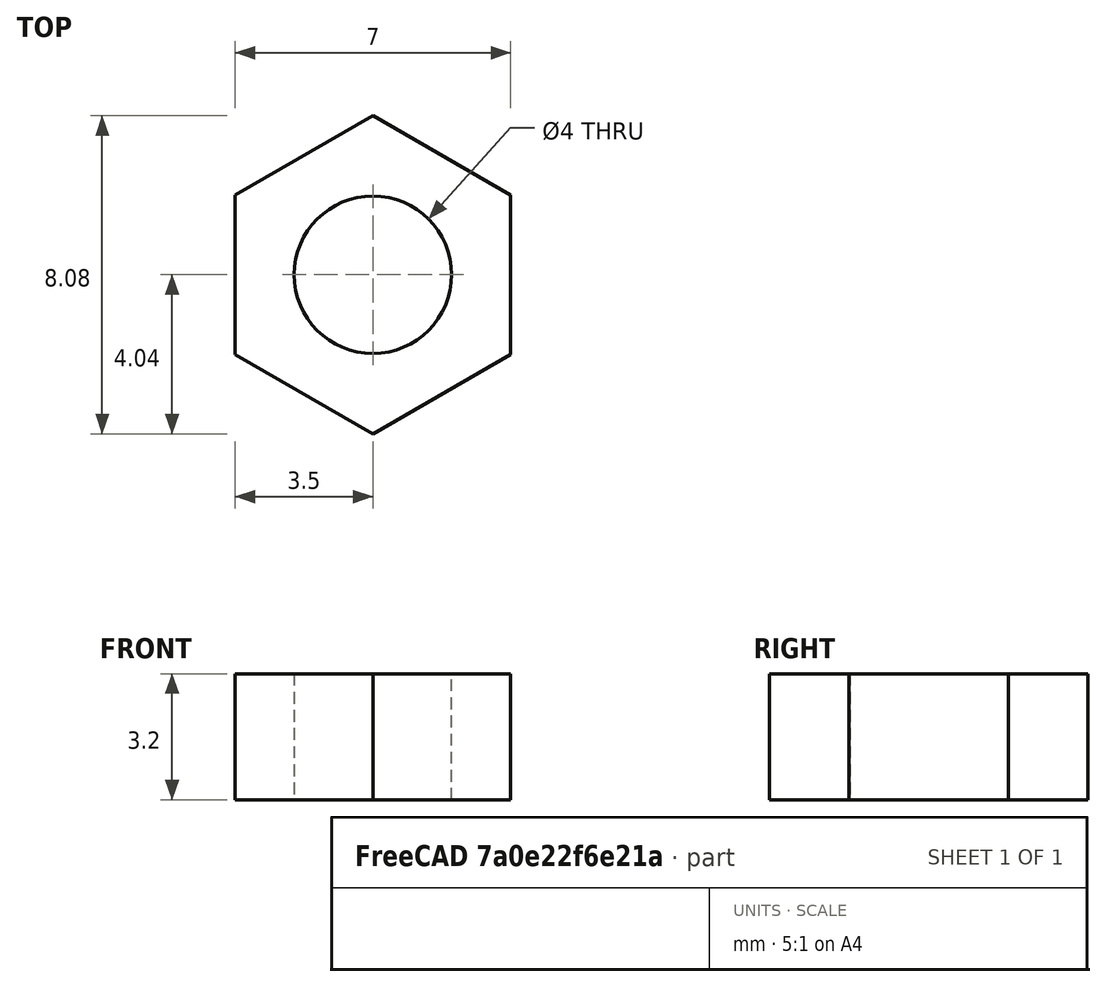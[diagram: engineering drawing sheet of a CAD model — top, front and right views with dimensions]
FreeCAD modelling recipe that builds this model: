
FCSTD DOCUMENT  (FreeCAD 0.18R14555 (Git shallow))
Label: m4-nut
License: All rights reserved
LicenseURL: http://en.wikipedia.org/wiki/All_rights_reserved
objects: Sketcher::SketchObject×1, PartDesign::Pad×1, PartDesign::Body×1
note: 4 computed .brp shape members not serialized (recipe doc carries the construction recipe); baked Part::Feature solids carry a one-line shape summary decoded from their .brp

FEATURE [Sketcher::SketchObject] Sketch
  MapMode = 5
  Support = -> [XY_Plane]
  sketch-geometry (8):
    g0: LineSegment StartX=3.5 StartY=2.02073 StartZ=0 EndX=-2.2e-15 EndY=4.04145 EndZ=0
    g1: LineSegment StartX=-2.2e-15 StartY=4.04145 StartZ=0 EndX=-3.5 EndY=2.02073 EndZ=0
    g2: LineSegment StartX=-3.5 StartY=2.02073 StartZ=0 EndX=-3.5 EndY=-2.02073 EndZ=0
    g3: LineSegment StartX=-3.5 StartY=-2.02073 StartZ=0 EndX=-1.24e-14 EndY=-4.04145 EndZ=0
    g4: LineSegment StartX=-1.24e-14 StartY=-4.04145 StartZ=0 EndX=3.5 EndY=-2.02073 EndZ=0
    g5: LineSegment StartX=3.5 StartY=-2.02073 StartZ=0 EndX=3.5 EndY=2.02073 EndZ=0
    g6: Circle [constr] CenterX=0 CenterY=0 CenterZ=0 NormalX=0 NormalY=0 NormalZ=1 AngleXU=0 Radius=4.04145
    g7: Circle CenterX=0 CenterY=0 CenterZ=0 NormalX=0 NormalY=0 NormalZ=1 AngleXU=0 Radius=2
  constraints (18):
    c: Coincident(g0,g1)
    c: Coincident(g1,g2)
    c: Coincident(g2,g3)
    c: Coincident(g3,g4)
    c: Coincident(g4,g5)
    c: Coincident(g5,g0)
    c: Equal(g0, g1-g5) x5
    c: PointOnObject(g0,g6)
    c: PointOnObject(g1,g6)
    c: PointOnObject(g2,g6)
    c: PointOnObject(g3,g6)
    c: PointOnObject(g4,g6)
    c: PointOnObject(g5,g6)
    c: Coincident(g6,g-1)
    c: Vertical(g5)
    c: DistanceX(g1,g0) = 7
    c: Coincident(g7,g-1)
    c: Radius(g7) = 2
FEATURE [PartDesign::Pad] Pad
  Length = 3.2
  Length2 = 100
  Profile = -> Sketch
  Type = 0
FEATURE [PartDesign::Body] Body
  Group = -> [Sketch,Pad]
  Origin = -> Origin
  Tip = -> Pad
